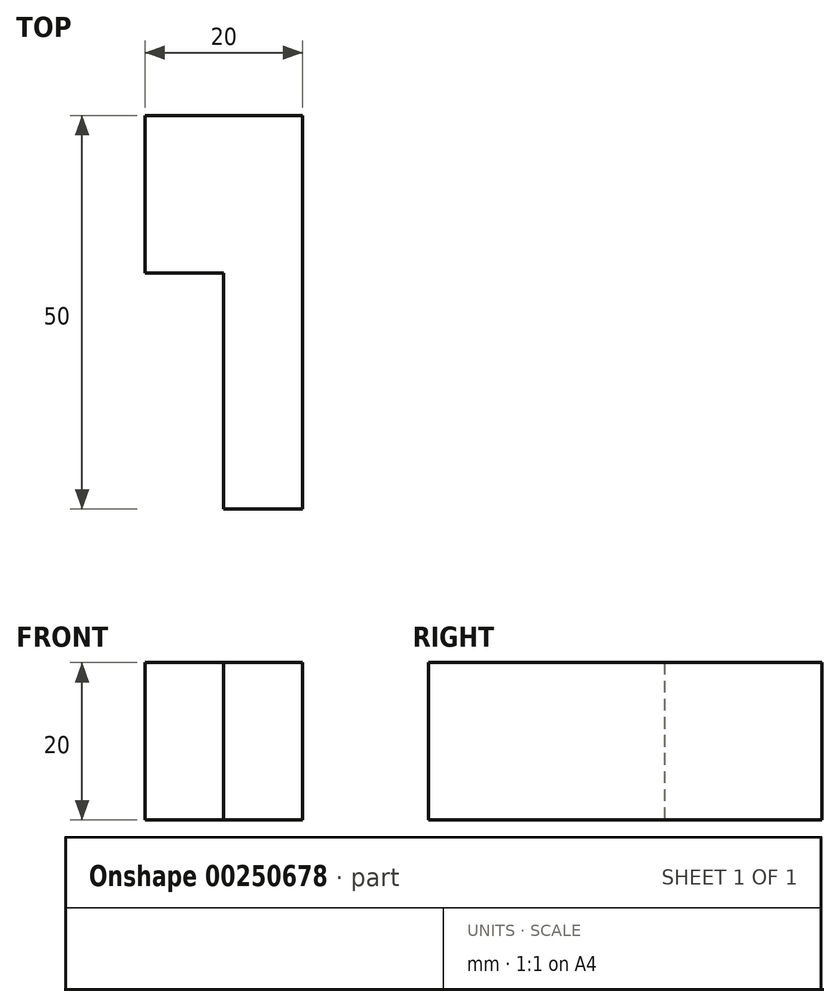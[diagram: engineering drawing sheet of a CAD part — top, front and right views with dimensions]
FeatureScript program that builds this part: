
annotation { "Feature Type Name" : "Feature", "Feature Type Description" : "" }
export const myFeature = defineFeature(function(context is Context, id is Id, definition is map)
    precondition{}
    {
        {
            var Q0;
            Q0=qCreatedBy(makeId("Top.planeOp"),FACE);
            var sketch = newSketch(context, id + "F0", { "sketchPlane" : qUnion([Q0])});
            skLineSegment(sketch, "E0.bottom", {"start": v(0, 20) * mm, "end": v(20, 20) * mm});
            skLineSegment(sketch, "E0.top", {"start": v(0, 0) * mm, "end": v(20, 0) * mm});
            skLineSegment(sketch, "E0.left", {"start": v(0, 20) * mm, "end": v(0, 0) * mm});
            skLineSegment(sketch, "E0.right", {"start": v(20, 20) * mm, "end": v(20, 0) * mm});
            skLineSegment(sketch, "E1.bottom", {"start": v(10, 0) * mm, "end": v(20, 0) * mm});
            skLineSegment(sketch, "E1.top", {"start": v(10, -30) * mm, "end": v(20, -30) * mm});
            skLineSegment(sketch, "E1.left", {"start": v(10, 0) * mm, "end": v(10, -30) * mm});
            skLineSegment(sketch, "E1.right", {"start": v(20, 0) * mm, "end": v(20, -30) * mm});
            skSolve(sketch);
        }
        {
            var Q0;
            Q0 = qSketchRegion(id + "F0", true);
            extrude(context, id + "F1", {"entities" : qUnion([Q0]), "depth" : 20 * mm});
        }
    });
